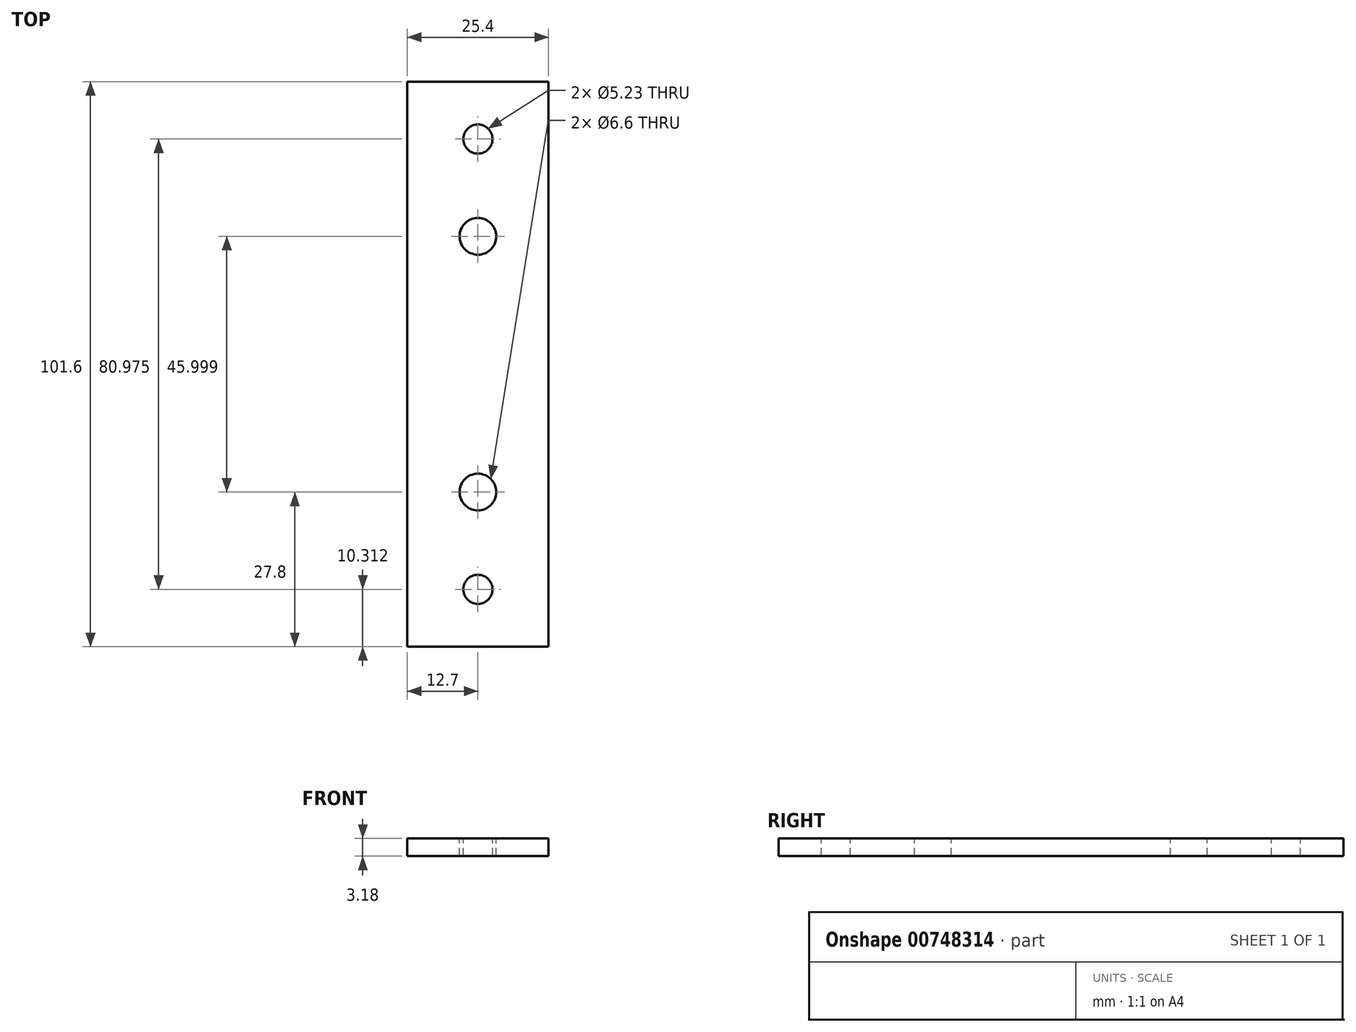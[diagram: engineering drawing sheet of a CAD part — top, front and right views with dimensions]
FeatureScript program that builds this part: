
annotation { "Feature Type Name" : "Feature", "Feature Type Description" : "" }
export const myFeature = defineFeature(function(context is Context, id is Id, definition is map)
    precondition{}
    {
        {
            var Q0;
            Q0=qCreatedBy(makeId("Front.planeOp"),FACE);
            var sketch = newSketch(context, id + "F0", { "sketchPlane" : qUnion([Q0])});
            skLineSegment(sketch, "E0.bottom", {"start": v(12.7, -1.59) * mm, "end": v(-12.7, -1.59) * mm});
            skLineSegment(sketch, "E0.top", {"start": v(12.7, 1.59) * mm, "end": v(-12.7, 1.59) * mm});
            skLineSegment(sketch, "E0.left", {"start": v(12.7, -1.59) * mm, "end": v(12.7, 1.59) * mm});
            skLineSegment(sketch, "E0.right", {"start": v(-12.7, -1.59) * mm, "end": v(-12.7, 1.59) * mm});
            skPoint(sketch, "E0.middle", {"position": v(0, 0) * mm});
            skSolve(sketch);
        }
        {
            var Q0;
            Q0=qSketchRegion(id+"F0",true);
            extrude(context, id + "F1", {"entities" : qUnion([Q0]), "depth" : 101.6 * mm, "offsetDistance" : 25.4 * mm});
        }
        {
            var Q0;
            Q0=makeQuery(id+"F1.opExtrude","SWEPT_FACE",FACE,{"disambiguationData":[OSD([sQuery(id+"F0.wireOp",EDGE,"E0.top")])]});
            var sketch = newSketch(context, id + "F2", { "sketchPlane" : qUnion([Q0])});
            skLineSegment(sketch, "E1", {"start": v(0, -101.6) * mm, "end": v(0, 0) * mm, "construction": true});
            skLineSegment(sketch, "E2", {"start": v(-12.7, -91.29) * mm, "end": v(12.7, -91.29) * mm, "construction": true});
            skLineSegment(sketch, "E3", {"start": v(-12.7, -10.31) * mm, "end": v(12.7, -10.31) * mm, "construction": true});
            skLineSegment(sketch, "E4", {"start": v(-12.7, -50.8) * mm, "end": v(12.7, -50.8) * mm, "construction": true});
            skCircle(sketch, "E5", {"center": v(0, -91.29) * mm, "radius": 2.62 * mm});
            skCircle(sketch, "E6", {"center": v(0, -10.31) * mm, "radius": 2.62 * mm});
            skPoint(sketch, "E7.middle", {"position": v(0, -50.8) * mm});
            skLineSegment(sketch, "E8.bottom", {"start": v(6.5, -27.8) * mm, "end": v(-6.5, -27.8) * mm, "construction": true});
            skLineSegment(sketch, "E8.top", {"start": v(6.5, -73.8) * mm, "end": v(-6.5, -73.8) * mm, "construction": true});
            skLineSegment(sketch, "E8.left", {"start": v(6.5, -27.8) * mm, "end": v(6.5, -73.8) * mm, "construction": true});
            skLineSegment(sketch, "E8.right", {"start": v(-6.5, -27.8) * mm, "end": v(-6.5, -73.8) * mm, "construction": true});
            skCircle(sketch, "E9", {"center": v(0, -73.8) * mm, "radius": 3.3 * mm});
            skCircle(sketch, "E10", {"center": v(0, -27.8) * mm, "radius": 3.3 * mm});
            skSolve(sketch);
        }
        {
            var Q0;
            Q0=qSketchRegion(id+"F2",true);
            extrude(context, id + "F3", {"entities" : qUnion([Q0]), "operationType" : NewBodyOperationType.REMOVE, "endBound" : BoundingType.THROUGH_ALL, "oppositeDirection" : true, "depth" : 25.4 * mm, "offsetDistance" : 25.4 * mm});
        }
    });
